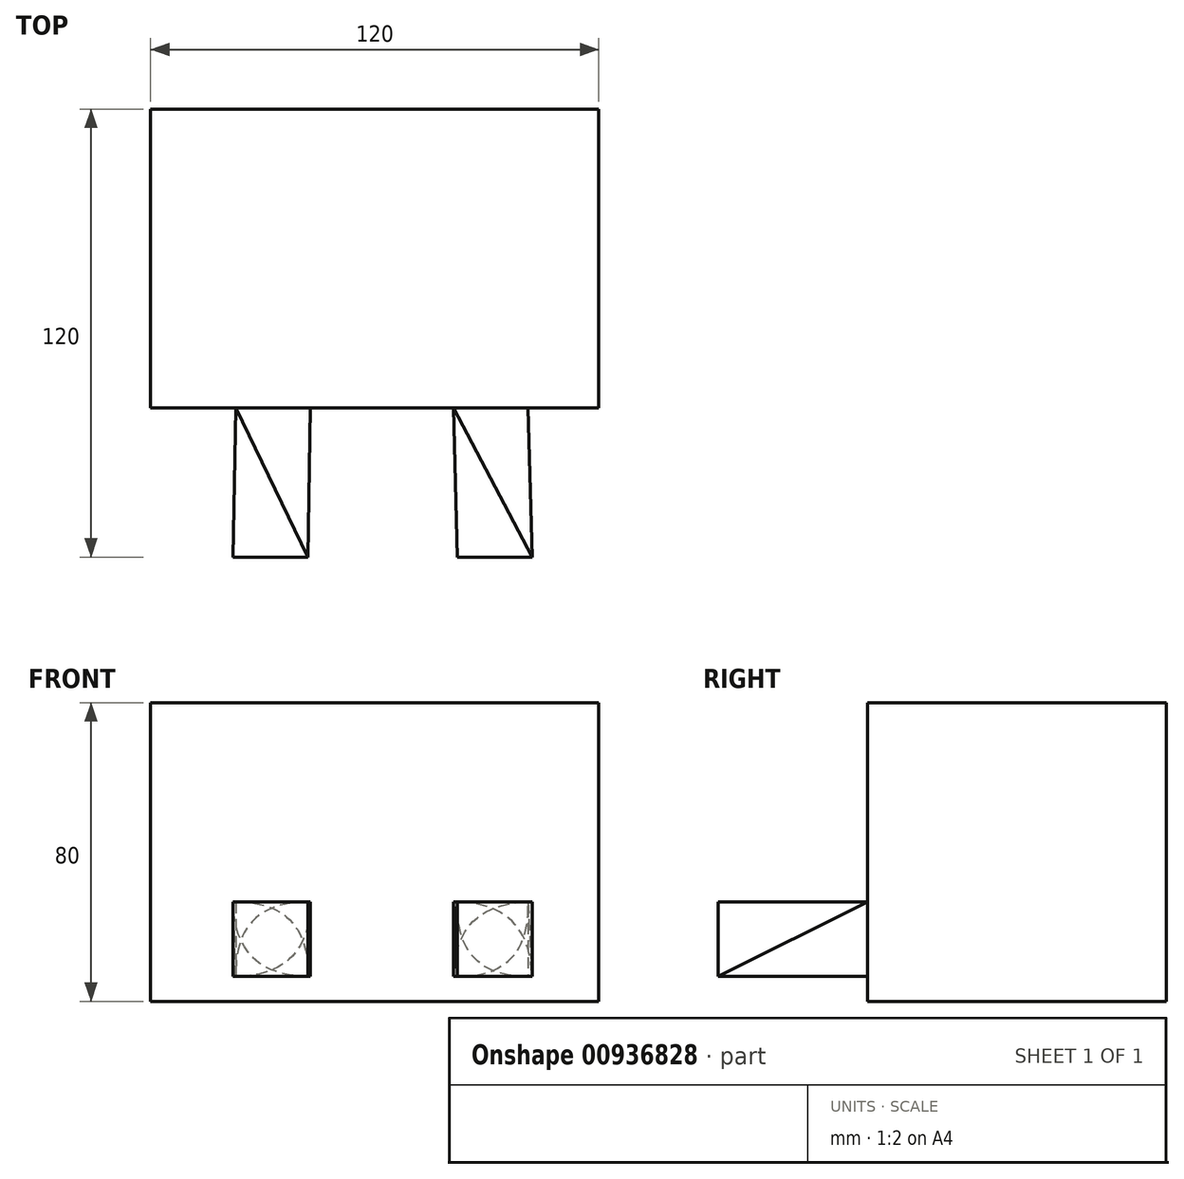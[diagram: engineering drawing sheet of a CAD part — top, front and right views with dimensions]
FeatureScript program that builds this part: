
annotation { "Feature Type Name" : "Feature", "Feature Type Description" : "" }
export const myFeature = defineFeature(function(context is Context, id is Id, definition is map)
    precondition{}
    {
        {
            var Q0;
            Q0=qCreatedBy(makeId("Front.planeOp"),FACE);
            var sketch = newSketch(context, id + "F0", { "sketchPlane" : qUnion([Q0])});
            skLineSegment(sketch, "E0.bottom", {"start": v(-51.23, 53.38) * mm, "end": v(68.77, 53.38) * mm});
            skLineSegment(sketch, "E0.top", {"start": v(-51.23, -26.62) * mm, "end": v(68.77, -26.62) * mm});
            skLineSegment(sketch, "E0.left", {"start": v(-51.23, 53.38) * mm, "end": v(-51.23, -26.62) * mm});
            skLineSegment(sketch, "E0.right", {"start": v(68.77, 53.38) * mm, "end": v(68.77, -26.62) * mm});
            skSolve(sketch);
        }
        {
            var Q0;
            Q0 = qSketchRegion(id + "F0", true);
            extrude(context, id + "F1", {"entities" : qUnion([Q0]), "depth" : 80 * mm, "offsetDistance" : 25 * mm});
        }
        {
            var Q0;
            Q0=makeQuery(id+"F1.opExtrude","CAP_FACE",FACE,{"disambiguationData":[OSD([sQuery(id+"F0.wireOp",EDGE,"E0.bottom"),sQuery(id+"F0.wireOp",EDGE,"E0.top"),sQuery(id+"F0.wireOp",EDGE,"E0.left"),sQuery(id+"F0.wireOp",EDGE,"E0.right")])],"isStart":false});
            var sketch = newSketch(context, id + "F2", { "sketchPlane" : qUnion([Q0])});
            skLineSegment(sketch, "E1", {"start": v(-28.47, 0) * mm, "end": v(-28.47, -20) * mm});
            skLineSegment(sketch, "E2", {"start": v(-28.47, -20) * mm, "end": v(-8.47, -20) * mm});
            skLineSegment(sketch, "E3", {"start": v(-8.47, -20) * mm, "end": v(-8.47, 0) * mm});
            skLineSegment(sketch, "E4", {"start": v(-8.47, 0) * mm, "end": v(-28.47, 0) * mm});
            skLineSegment(sketch, "E5.bottom", {"start": v(29.85, 0) * mm, "end": v(49.85, 0) * mm});
            skLineSegment(sketch, "E5.top", {"start": v(29.85, -20) * mm, "end": v(49.85, -20) * mm});
            skLineSegment(sketch, "E5.left", {"start": v(29.85, 0) * mm, "end": v(29.85, -20) * mm});
            skLineSegment(sketch, "E5.right", {"start": v(49.85, 0) * mm, "end": v(49.85, -20) * mm});
            skSolve(sketch);
        }
        {
            var Q0;
            Q0=qCreatedBy(makeId("Front.planeOp"),FACE);
            cPlane(context, id + "F3", {"entities" : qUnion([Q0]), "cplaneType" : CPlaneType.OFFSET, "offset" : 120 * mm, "width" : 150 * mm, "height" : 150 * mm});
        }
        {
            var Q0;
            Q0=qCreatedBy(id+"F3.planeOp",FACE);
            var sketch = newSketch(context, id + "F4", { "sketchPlane" : qUnion([Q0])});
            skLineSegment(sketch, "E6.bottom", {"start": v(-29.14, 0) * mm, "end": v(-9.14, 0) * mm});
            skLineSegment(sketch, "E6.top", {"start": v(-29.14, -20) * mm, "end": v(-9.14, -20) * mm});
            skLineSegment(sketch, "E6.left", {"start": v(-29.14, 0) * mm, "end": v(-29.14, -20) * mm});
            skLineSegment(sketch, "E6.right", {"start": v(-9.14, 0) * mm, "end": v(-9.14, -20) * mm});
            skLineSegment(sketch, "E7.bottom", {"start": v(30.89, 0) * mm, "end": v(50.89, 0) * mm});
            skLineSegment(sketch, "E7.top", {"start": v(30.89, -20) * mm, "end": v(50.89, -20) * mm});
            skLineSegment(sketch, "E7.left", {"start": v(30.89, 0) * mm, "end": v(30.89, -20) * mm});
            skLineSegment(sketch, "E7.right", {"start": v(50.89, 0) * mm, "end": v(50.89, -20) * mm});
            skSolve(sketch);
        }
        {
            var Q1;
            Q1=makeQuery(id+"F2.imprint","IMPRINT",FACE,{"disambiguationData":[TD([[makeQuery(id+"F2.imprint","IMPRINT",EDGE,{"derivedFrom":sQuery(id+"F2.wireOp",EDGE,"E1")}),1.0]])]});
            var Q2;
            Q2=makeQuery(id+"F4.imprint","IMPRINT",FACE,{"disambiguationData":[TD([[makeQuery(id+"F4.imprint","IMPRINT",EDGE,{"derivedFrom":sQuery(id+"F4.wireOp",EDGE,"E6.bottom")}),-1.0]])]});
            var Q3;
            Q3=sQuery(id+"F2.wireOp",VERTEX,"E1.end");
            var Q4;
            Q4=sQuery(id+"F4.wireOp",VERTEX,"E6.bottom.start");
            loft(context, id + "F5", {"operationType" : NewBodyOperationType.ADD, "sheetProfilesArray" : [{ "sheetProfileEntities" : qUnion([Q1]) }, { "sheetProfileEntities" : qUnion([Q2]) }], "matchConnections" : true, "connections" : [{ "connectionEntities" : qUnion([Q3, Q4]), "connectionEdgeQueries" : qUnion([]), "connectionEdgeParameters" : [] }]});
        }
        {
            var Q1;
            Q1=makeQuery(id+"F2.imprint","IMPRINT",FACE,{"disambiguationData":[TD([[makeQuery(id+"F2.imprint","IMPRINT",EDGE,{"derivedFrom":sQuery(id+"F2.wireOp",EDGE,"E5.bottom")}),-1.0]])]});
            var Q2;
            Q2=makeQuery(id+"F4.imprint","IMPRINT",FACE,{"disambiguationData":[TD([[makeQuery(id+"F4.imprint","IMPRINT",EDGE,{"derivedFrom":sQuery(id+"F4.wireOp",EDGE,"E7.bottom")}),-1.0]])]});
            var Q3;
            Q3=sQuery(id+"F2.wireOp",VERTEX,"E5.bottom.start");
            var Q4;
            Q4=sQuery(id+"F4.wireOp",VERTEX,"E7.bottom.end");
            loft(context, id + "F6", {"operationType" : NewBodyOperationType.ADD, "sheetProfilesArray" : [{ "sheetProfileEntities" : qUnion([Q1]) }, { "sheetProfileEntities" : qUnion([Q2]) }], "matchConnections" : true, "connections" : [{ "connectionEntities" : qUnion([Q3, Q4]), "connectionEdgeQueries" : qUnion([]), "connectionEdgeParameters" : [] }]});
        }
    });
